annotation { "Feature Type Name" : "Feature", "Feature Type Description" : "" }
export const myFeature = defineFeature(function(context is Context, id is Id, definition is map)
    precondition{}
    {
        {
            var Q0;
            Q0=qCreatedBy(makeId("Top.planeOp"),FACE);
            var sketch = newSketch(context, id + "F0", { "sketchPlane" : qUnion([Q0])});
            skLineSegment(sketch, "E0", {"start": v(-15.02, 7.4) * mm, "end": v(-34.2, 7.4) * mm});
            skLineSegment(sketch, "E1", {"start": v(-34.2, 7.4) * mm, "end": v(-34.2, 8.8) * mm});
            skLineSegment(sketch, "E2", {"start": v(-33.6, 9.4) * mm, "end": v(-25.35, 9.4) * mm});
            skLineSegment(sketch, "E3", {"start": v(-21.54, 14.63) * mm, "end": v(-22.83, 18.6) * mm});
            skLineSegment(sketch, "E4", {"start": v(-22.26, 19.4) * mm, "end": v(-21.82, 19.4) * mm});
            skLineSegment(sketch, "E5", {"start": v(-20.87, 18.7) * mm, "end": v(-18.58, 11.67) * mm});
            skLineSegment(sketch, "E6", {"start": v(-18.2, 11.4) * mm, "end": v(-18.04, 11.4) * mm});
            skLineSegment(sketch, "E7", {"start": v(-17.66, 11.92) * mm, "end": v(-19.8, 18.48) * mm});
            skLineSegment(sketch, "E8", {"start": v(-19.13, 19.4) * mm, "end": v(-18.6, 19.4) * mm});
            skLineSegment(sketch, "E9", {"start": v(-17.93, 18.91) * mm, "end": v(-14.45, 8.18) * mm});
            skPoint(sketch, "E10.visualSharp", {"position": v(-19.84, 9.4) * mm});
            skArc(sketch, "E10.filletArc", {"start": v(-25.35, 9.4) * mm, "mid": v(-22.1, 11.04) * mm, "end": v(-21.54, 14.63) * mm});
            skPoint(sketch, "E11.visualSharp", {"position": v(-17.5, 11.4) * mm});
            skArc(sketch, "E11.filletArc", {"start": v(-18.04, 11.4) * mm, "mid": v(-17.72, 11.56) * mm, "end": v(-17.66, 11.92) * mm});
            skPoint(sketch, "E12.visualSharp", {"position": v(-18.5, 11.4) * mm});
            skArc(sketch, "E12.filletArc", {"start": v(-18.58, 11.67) * mm, "mid": v(-18.43, 11.47) * mm, "end": v(-18.2, 11.4) * mm});
            skPoint(sketch, "E13.visualSharp", {"position": v(-21.09, 19.4) * mm});
            skArc(sketch, "E13.filletArc", {"start": v(-20.87, 18.7) * mm, "mid": v(-21.23, 19.2) * mm, "end": v(-21.82, 19.4) * mm});
            skPoint(sketch, "E14.visualSharp", {"position": v(-20.09, 19.4) * mm});
            skArc(sketch, "E14.filletArc", {"start": v(-19.13, 19.4) * mm, "mid": v(-19.7, 19.1) * mm, "end": v(-19.8, 18.48) * mm});
            skPoint(sketch, "E15.visualSharp", {"position": v(-18.09, 19.4) * mm});
            skArc(sketch, "E15.filletArc", {"start": v(-17.93, 18.91) * mm, "mid": v(-18.19, 19.26) * mm, "end": v(-18.6, 19.4) * mm});
            skPoint(sketch, "E16.visualSharp", {"position": v(-23.09, 19.4) * mm});
            skArc(sketch, "E16.filletArc", {"start": v(-22.26, 19.4) * mm, "mid": v(-22.75, 19.15) * mm, "end": v(-22.83, 18.6) * mm});
            skPoint(sketch, "E17.visualSharp", {"position": v(-34.2, 9.4) * mm});
            skArc(sketch, "E17.filletArc", {"start": v(-33.6, 9.4) * mm, "mid": v(-34.01, 9.22) * mm, "end": v(-34.2, 8.8) * mm});
            skPoint(sketch, "E18.visualSharp", {"position": v(-14.2, 7.4) * mm});
            skArc(sketch, "E18.filletArc", {"start": v(-15.02, 7.4) * mm, "mid": v(-14.53, 7.64) * mm, "end": v(-14.45, 8.18) * mm});
            skSolve(sketch);
        }
        {
            var Q0;
            Q0 = qSketchRegion(id + "F0", true);
            extrude(context, id + "F1", {"entities" : qUnion([Q0]), "depth" : 40 * mm, "offsetDistance" : 25 * mm});
        }
        {
            var Q0;
            Q0=makeQuery(id+"F1.opExtrude","SWEPT_FACE",FACE,{"disambiguationData":[OSD([sQuery(id+"F0.wireOp",EDGE,"E9")])]});
            var sketch = newSketch(context, id + "F2", { "sketchPlane" : qUnion([Q0])});
            skText(sketch, "E19", { "text": "Scout Law", "fontName": "OpenSans-Bold.ttf"});
            skLineSegment(sketch, "E20", {"start": v(14.74, 40) * mm, "end": v(14.74, 0) * mm, "construction": true});
            skLineSegment(sketch, "E21", {"start": v(23.53, 20) * mm, "end": v(12.24, 20) * mm, "construction": true});
            const initialGuessF2  = {"E19": [0.01673, 0.037, 0, -1, 0.00479]};
            skSetInitialGuess(sketch, initialGuessF2);
            skSolve(sketch);
        }
        {
            var Q0;
            Q0=makeQuery(id+"F2.imprint","IMPRINT",FACE,{"disambiguationData":[TD([[makeQuery(id+"F2.imprint","IMPRINT",EDGE,{"derivedFrom":sQuery(id+"F2.wireOp",EDGE,"E19.sketch_text.stroke-0")}),-1.0]])]});
            var Q1;
            Q1=makeQuery(id+"F2.imprint","IMPRINT",FACE,{"disambiguationData":[TD([[makeQuery(id+"F2.imprint","IMPRINT",EDGE,{"derivedFrom":sQuery(id+"F2.wireOp",EDGE,"E19.sketch_text.stroke-28")}),-1.0]])]});
            var Q2;
            Q2=makeQuery(id+"F2.imprint","IMPRINT",FACE,{"disambiguationData":[TD([[makeQuery(id+"F2.imprint","IMPRINT",EDGE,{"derivedFrom":sQuery(id+"F2.wireOp",EDGE,"E19.sketch_text.stroke-42")}),-1.0]])]});
            var Q3;
            Q3=makeQuery(id+"F2.imprint","IMPRINT",FACE,{"disambiguationData":[TD([[makeQuery(id+"F2.imprint","IMPRINT",EDGE,{"derivedFrom":sQuery(id+"F2.wireOp",EDGE,"E19.sketch_text.stroke-60")}),-1.0]])]});
            var Q4;
            Q4=makeQuery(id+"F2.imprint","IMPRINT",FACE,{"disambiguationData":[TD([[makeQuery(id+"F2.imprint","IMPRINT",EDGE,{"derivedFrom":sQuery(id+"F2.wireOp",EDGE,"E19.sketch_text.stroke-77")}),-1.0]])]});
            var Q5;
            Q5=makeQuery(id+"F2.imprint","IMPRINT",FACE,{"disambiguationData":[TD([[makeQuery(id+"F2.imprint","IMPRINT",EDGE,{"derivedFrom":sQuery(id+"F2.wireOp",EDGE,"E19.sketch_text.stroke-95")}),-1.0]])]});
            var Q6;
            Q6=makeQuery(id+"F2.imprint","IMPRINT",FACE,{"disambiguationData":[TD([[makeQuery(id+"F2.imprint","IMPRINT",EDGE,{"derivedFrom":sQuery(id+"F2.wireOp",EDGE,"E19.sketch_text.stroke-101")}),-1.0]])]});
            var Q7;
            Q7=makeQuery(id+"F2.imprint","IMPRINT",FACE,{"disambiguationData":[TD([[makeQuery(id+"F2.imprint","IMPRINT",EDGE,{"derivedFrom":sQuery(id+"F2.wireOp",EDGE,"E19.sketch_text.stroke-126")}),-1.0]])]});
            extrude(context, id + "F3", {"entities" : qUnion([Q0, Q1, Q2, Q3, Q4, Q5, Q6, Q7]), "operationType" : NewBodyOperationType.REMOVE, "oppositeDirection" : true, "depth" : 1 * mm, "offsetDistance" : 25 * mm});
        }
    });